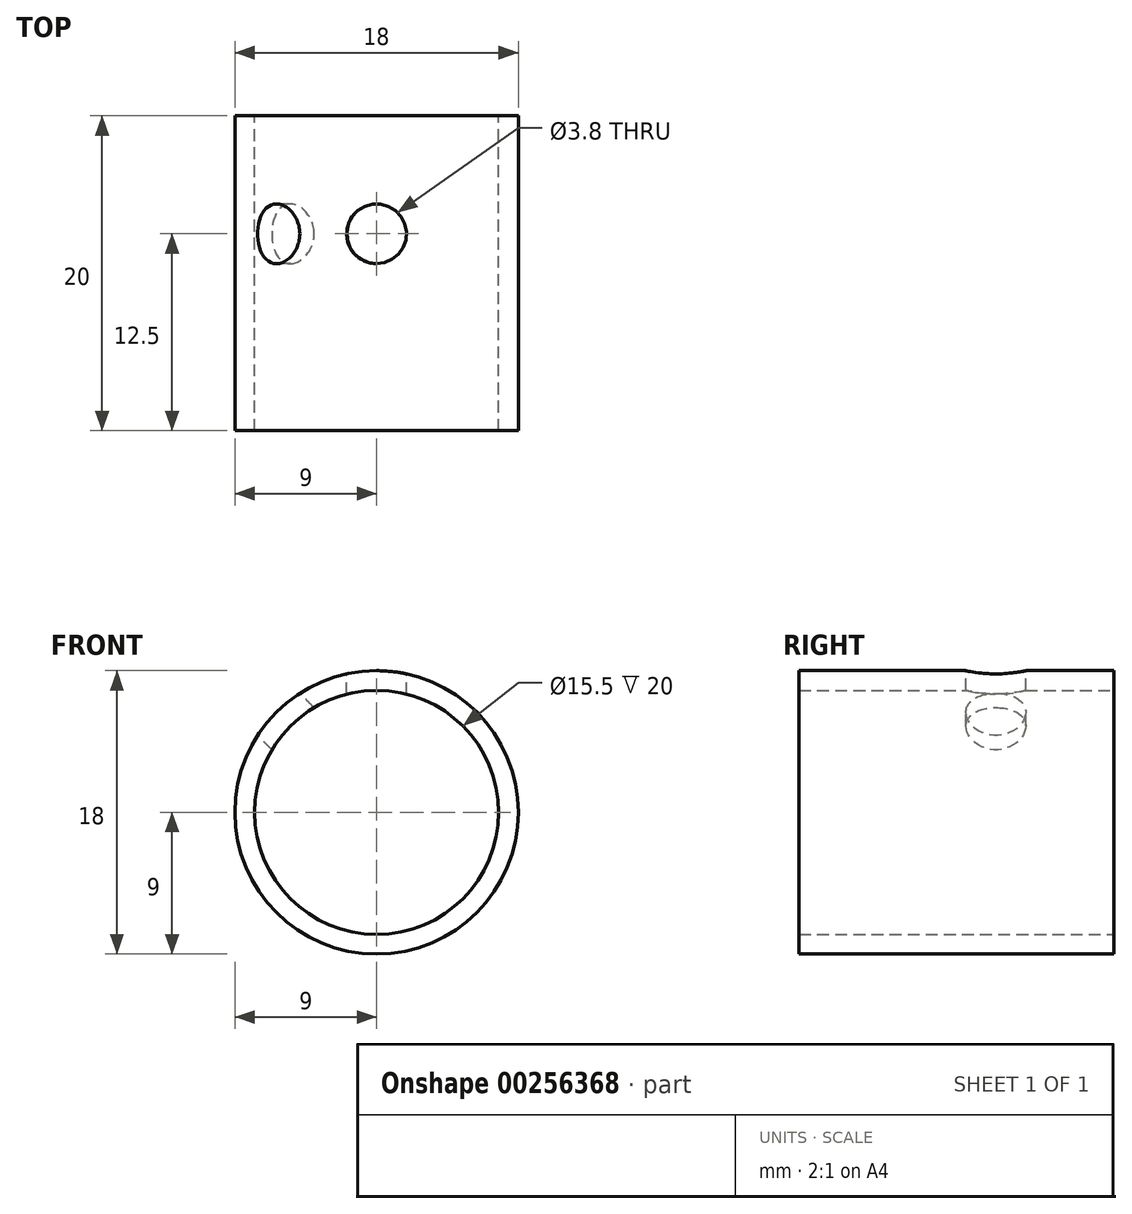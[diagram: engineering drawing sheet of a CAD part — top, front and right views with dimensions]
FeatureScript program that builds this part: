
annotation { "Feature Type Name" : "Feature", "Feature Type Description" : "" }
export const myFeature = defineFeature(function(context is Context, id is Id, definition is map)
    precondition{}
    {
        {
            var Q0;
            Q0=qCreatedBy(makeId("Front.planeOp"),FACE);
            var sketch = newSketch(context, id + "F0", { "sketchPlane" : qUnion([Q0])});
            skCircle(sketch, "E0", {"center": v(0, 0) * mm, "radius": 9 * mm});
            skCircle(sketch, "E1", {"center": v(0, 0) * mm, "radius": 7.75 * mm});
            skSolve(sketch);
        }
        {
            var Q0;
            Q0 = qSketchRegion(id + "F0", true);
            extrude(context, id + "F1", {"entities" : qUnion([Q0]), "depth" : 20 * mm});
        }
        {
            var Q0;
            Q0=qCreatedBy(makeId("Top.planeOp"),FACE);
            cPlane(context, id + "F2", {"entities" : qUnion([Q0]), "cplaneType" : CPlaneType.OFFSET, "offset" : 9 * mm, "width" : 150 * mm, "height" : 150 * mm});
        }
        {
            var Q0;
            Q0=qCreatedBy(id+"F2.planeOp",FACE);
            var sketch = newSketch(context, id + "F3", { "sketchPlane" : qUnion([Q0])});
            skPoint(sketch, "E2", {"position": v(0, -7.5) * mm});
            skSolve(sketch);
        }
        {
            var Q0;
            Q0=sQuery(id+"F3.wireOp",VERTEX,"E2");
            var Q1;
            Q1=makeQuery(id+"F1.opExtrude","SWEPT_BODY",BODY,{"disambiguationData":[OSD([sQuery(id+"F0.wireOp",EDGE,"E0"),sQuery(id+"F0.wireOp",EDGE,"E1")])]});
            hole(context, id + "F4", {"style" : HoleStyle.SIMPLE, "endStyle" : HoleEndStyle.BLIND, "standardTappedOrClearance" : lookupTablePath({ "standard" : "ANSI", "fit" : "Normal (ASME)", "size" : "#6", "type" : "Clearance" }), "standardBlindInLast" : lookupTablePath({ "fit" : "Free", "standard" : "ANSI", "size" : "#6", "type" : "Clearance" }), "holeDiameter" : 3.8 * mm, "holeDepth" : 3.02 * mm, "tappedDepth" : 0.64 * mm, "tapClearance" : 3, "locations" : qUnion([Q0]), "scope" : qUnion([Q1])});
        }
        {
            var Q0;
            Q0=qCreatedBy(makeId("Front.planeOp"),FACE);
            var sketch = newSketch(context, id + "F5", { "sketchPlane" : qUnion([Q0])});
            skLineSegment(sketch, "E3", {"start": v(0, 0) * mm, "end": v(-6.36, 6.36) * mm});
            skLineSegment(sketch, "E4", {"start": v(-6.36, 6.36) * mm, "end": v(-12.73, 0) * mm});
            skSolve(sketch);
        }
        {
            var Q0;
            Q0=qCreatedBy(makeId("Right.planeOp"),FACE);
            var Q1;
            Q1=sQuery(id+"F5.wireOp",EDGE,"E4");
            cPlane(context, id + "F6", {"entities" : qUnion([Q0, Q1]), "cplaneType" : CPlaneType.LINE_ANGLE, "offset" : 25 * mm, "angle" : 0 * degree, "oppositeDirection" : true, "width" : 150 * mm, "height" : 150 * mm});
        }
        {
            var Q0;
            Q0=qCreatedBy(id+"F6.planeOp",FACE);
            var sketch = newSketch(context, id + "F7", { "sketchPlane" : qUnion([Q0])});
            skCircle(sketch, "E5", {"center": v(7.5, 0) * mm, "radius": 4.22 * mm});
            skSolve(sketch);
        }
        {
            var Q0;
            Q0=sQuery(id+"F7.wireOp",VERTEX,"E5.center");
            var Q1;
            Q1=makeQuery(id+"F1.opExtrude","SWEPT_BODY",BODY,{"disambiguationData":[OSD([sQuery(id+"F0.wireOp",EDGE,"E0"),sQuery(id+"F0.wireOp",EDGE,"E1")])]});
            hole(context, id + "F8", {"style" : HoleStyle.SIMPLE, "endStyle" : HoleEndStyle.BLIND, "standardTappedOrClearance" : lookupTablePath({ "standard" : "ANSI", "fit" : "Normal (ASME)", "size" : "#6", "type" : "Clearance" }), "standardBlindInLast" : lookupTablePath({ "fit" : "Free", "standard" : "ANSI", "size" : "#6", "type" : "Clearance" }), "holeDiameter" : 3.8 * mm, "holeDepth" : 2 * mm, "tappedDepth" : 12 * mm, "tapClearance" : 3, "locations" : qUnion([Q0]), "scope" : qUnion([Q1])});
        }
    });
